# Revit family: STC_A3-Pipe
name_source: partatom
category: Structural Columns
revit_build: Autodesk Revit 2016 (Build: 20150220_1215(x64)
units: mm (PartAtom-declared; Revit-internal decimal feet)

## family parameters
Always export as geometry = No
Beam cutback in plan = From bounding box
Cut with Voids When Loaded = No
Material for Model Behavior = Steel
Section Shape = Not Defined
Shared = No
Show family pre-cut in plan views = Yes

## types (2) — shared parameters
Gauge = Standard
Keynote = G10

## per-type parameters (varying)
| type | A | ID | OD | W | t |
| PIPE102STD Pipe | 2050 m² | 102 mm | 114 mm  [stored 0.374016 ft] | 0.158 | 6 mm  [stored 0.019685 ft] |
| PIPE152STD Pipe | 3600 m² | 154 mm  [stored 0.505249 ft] | 168 mm  [stored 0.551181 ft] | 0.277 | 7 mm  [stored 0.0229659 ft] |

note: [stored X ft] marks values corroborated as IEEE doubles in the binary element streams (Revit-internal decimal feet)

## geometry (parser evidence)
native form markers: Sweep x1
no freeform markers — native parametric forms only
